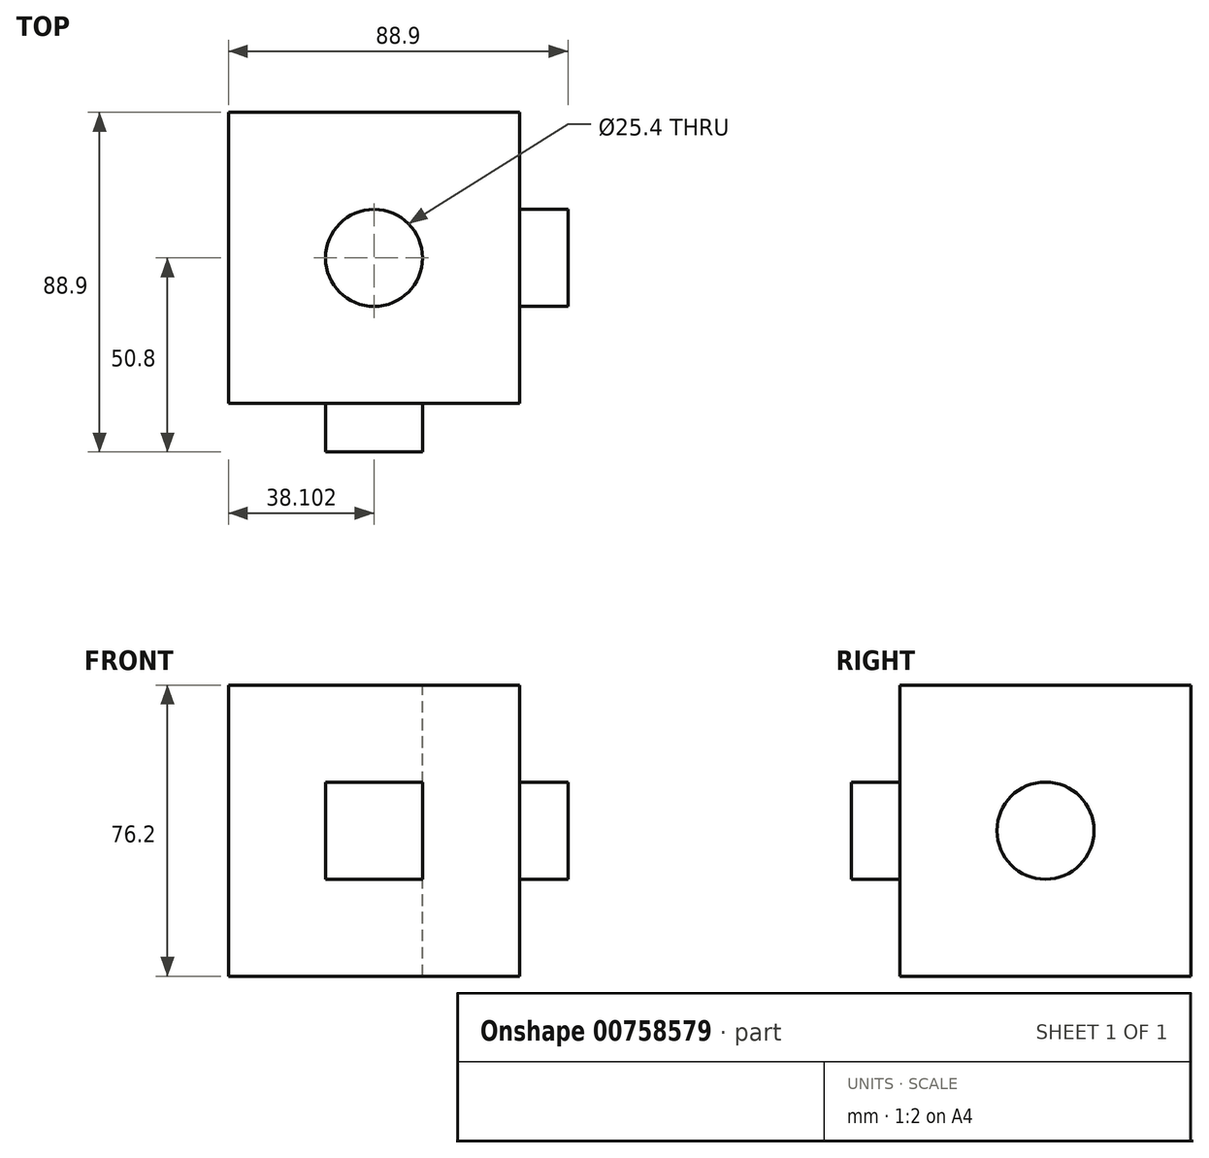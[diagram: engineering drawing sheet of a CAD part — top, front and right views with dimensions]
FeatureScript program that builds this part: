
annotation { "Feature Type Name" : "Feature", "Feature Type Description" : "" }
export const myFeature = defineFeature(function(context is Context, id is Id, definition is map)
    precondition{}
    {
        {
            var Q0;
            Q0=qCreatedBy(makeId("Front.planeOp"),FACE);
            var sketch = newSketch(context, id + "F0", { "sketchPlane" : qUnion([Q0])});
            skLineSegment(sketch, "E0.bottom", {"start": v(-35.93, -26.45) * mm, "end": v(40.27, -26.45) * mm});
            skLineSegment(sketch, "E0.top", {"start": v(-35.93, 49.75) * mm, "end": v(40.27, 49.75) * mm});
            skLineSegment(sketch, "E0.left", {"start": v(-35.93, -26.45) * mm, "end": v(-35.93, 49.75) * mm});
            skLineSegment(sketch, "E0.right", {"start": v(40.27, -26.45) * mm, "end": v(40.27, 49.75) * mm});
            skSolve(sketch);
        }
        {
            var Q0;
            Q0=makeQuery(id+"F0.imprint","IMPRINT",FACE,{"disambiguationData":[TD([[makeQuery(id+"F0.imprint","IMPRINT",EDGE,{"derivedFrom":sQuery(id+"F0.wireOp",EDGE,"E0.bottom")}),1.0]])]});
            extrude(context, id + "F1", {"entities" : qUnion([Q0]), "depth" : 76.2 * mm, "offsetDistance" : 25.4 * mm});
        }
        {
            var Q0;
            Q0=makeQuery(id+"F1.opExtrude","CAP_FACE",FACE,{"disambiguationData":[OSD([sQuery(id+"F0.wireOp",EDGE,"E0.bottom"),sQuery(id+"F0.wireOp",EDGE,"E0.top"),sQuery(id+"F0.wireOp",EDGE,"E0.left"),sQuery(id+"F0.wireOp",EDGE,"E0.right")])],"isStart":false});
            var sketch = newSketch(context, id + "F2", { "sketchPlane" : qUnion([Q0])});
            skLineSegment(sketch, "E1.bottom", {"start": v(-10.53, -1.05) * mm, "end": v(14.87, -1.05) * mm});
            skLineSegment(sketch, "E1.top", {"start": v(-10.53, 24.35) * mm, "end": v(14.87, 24.35) * mm});
            skLineSegment(sketch, "E1.left", {"start": v(-10.53, -1.05) * mm, "end": v(-10.53, 24.35) * mm});
            skLineSegment(sketch, "E1.right", {"start": v(14.87, -1.05) * mm, "end": v(14.87, 24.35) * mm});
            skSolve(sketch);
        }
        {
            var Q0;
            Q0=makeQuery(id+"F2.imprint","IMPRINT",FACE,{"disambiguationData":[TD([[makeQuery(id+"F2.imprint","IMPRINT",EDGE,{"derivedFrom":sQuery(id+"F2.wireOp",EDGE,"E1.bottom")}),1.0]])]});
            extrude(context, id + "F3", {"entities" : qUnion([Q0]), "operationType" : NewBodyOperationType.ADD, "depth" : 12.7 * mm, "offsetDistance" : 25.4 * mm});
        }
        {
            var Q0;
            Q0=makeQuery(id+"F1.opExtrude","SWEPT_FACE",FACE,{"disambiguationData":[OSD([sQuery(id+"F0.wireOp",EDGE,"E0.right")])]});
            var sketch = newSketch(context, id + "F4", { "sketchPlane" : qUnion([Q0])});
            skCircle(sketch, "E2", {"center": v(-38.1, 11.65) * mm, "radius": 12.7 * mm});
            skSolve(sketch);
        }
        {
            var Q0;
            Q0 = qSketchRegion(id + "F4", true);
            extrude(context, id + "F5", {"entities" : qUnion([Q0]), "operationType" : NewBodyOperationType.ADD, "depth" : 12.7 * mm, "offsetDistance" : 25.4 * mm});
        }
        {
            var Q0;
            Q0=makeQuery(id+"F1.opExtrude","SWEPT_FACE",FACE,{"disambiguationData":[OSD([sQuery(id+"F0.wireOp",EDGE,"E0.top")])]});
            var sketch = newSketch(context, id + "F6", { "sketchPlane" : qUnion([Q0])});
            skPoint(sketch, "E3", {"position": v(2.17, -38.1) * mm});
            skSolve(sketch);
        }
        {
            var Q0;
            Q0=sQuery(id+"F6.wireOp",VERTEX,"E3");
            var Q1;
            Q1=makeQuery(id+"F1.opExtrude","SWEPT_BODY",BODY,{"disambiguationData":[OSD([sQuery(id+"F0.wireOp",EDGE,"E0.bottom"),sQuery(id+"F0.wireOp",EDGE,"E0.top"),sQuery(id+"F0.wireOp",EDGE,"E0.left"),sQuery(id+"F0.wireOp",EDGE,"E0.right")])]});
            hole(context, id + "F7", {"style" : HoleStyle.SIMPLE, "endStyle" : HoleEndStyle.THROUGH, "holeDiameter" : 25.4 * mm, "majorDiameter" : 6.35 * mm, "isTappedThrough" : true, "tappedDepth" : 12.7 * mm, "tapClearance" : 3, "locations" : qUnion([Q0]), "scope" : qUnion([Q1])});
        }
    });
